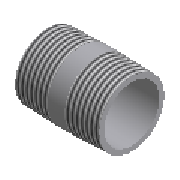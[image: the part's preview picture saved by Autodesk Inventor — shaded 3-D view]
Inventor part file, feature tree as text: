
AUTODESK INVENTOR PART (.ipt)
format: ipt  version: 2023.2 (Build 272271030, 271C)  size: 180,736 bytes
history: native  units: mm (DEFAULTED — no unit token found)
features: other x6, revolve x1, sketch x1
ambient origin geometry x8: Origin, YZ Plane, XZ Plane, XY Plane, X Axis, Y Axis, Z Axis, Center Point
bodies: Solid1 (feature_tree)
feature tree (8):
  revolve  "Revolution1"  [1 undecoded]
  other  "Work Point3"
  other  "Work Point4"
  other  "Work Axis1"
  other  "Work Point5"
  other  "Work Axis2"
  other  "Work Point6"
  sketch  "Sketch1"  dims[d12=90.0deg d1=0.312398mm d2=50.0mm d3=22.5mm d4=0.0mm d5=22.5mm d6=0.0mm d7=12.7mm d8=41.91mm d57=35.7mm d60=19.1mm d62=0.0mm]
note: 1 required parameter value undecoded (feature->parameter linkage not recoverable at this tier; creation-order binding heuristic only, values carry confidence <= 0.55)
